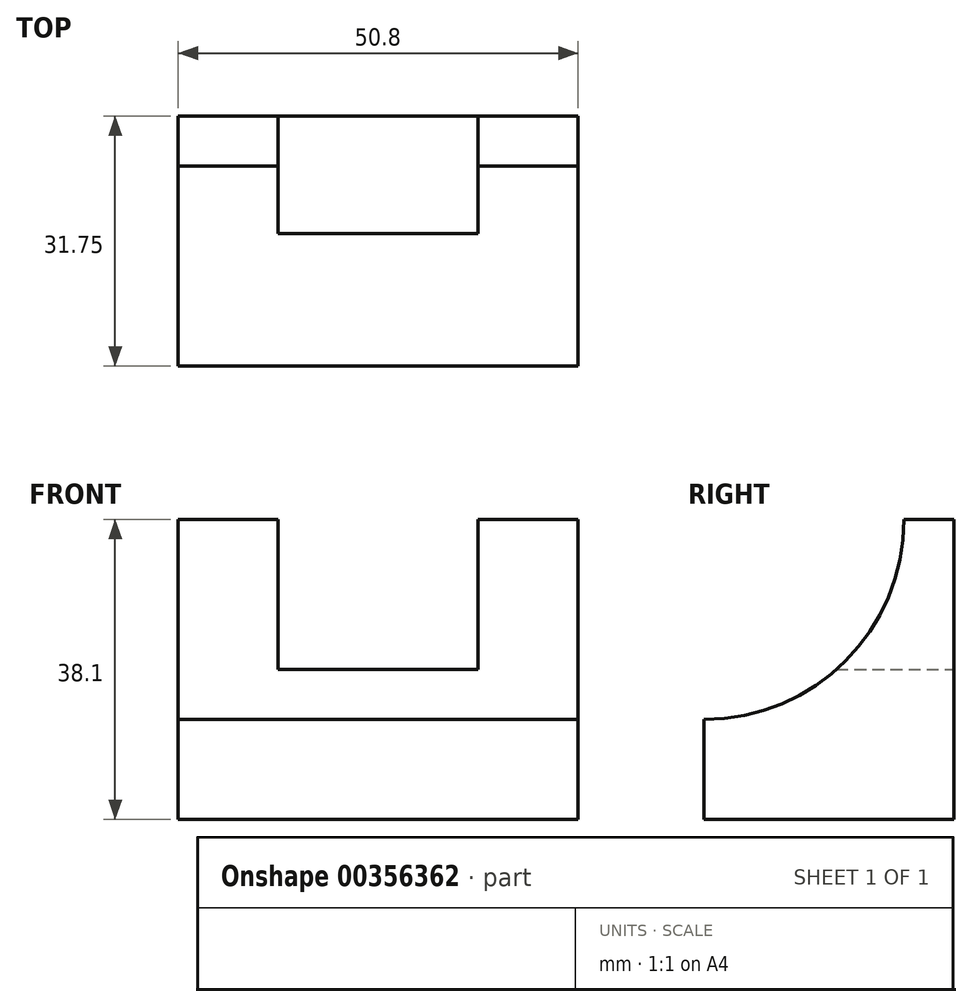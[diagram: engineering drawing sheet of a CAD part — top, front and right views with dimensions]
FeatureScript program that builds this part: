
annotation { "Feature Type Name" : "Feature", "Feature Type Description" : "" }
export const myFeature = defineFeature(function(context is Context, id is Id, definition is map)
    precondition{}
    {
        {
            var Q0;
            Q0=qCreatedBy(makeId("Right.planeOp"),FACE);
            var sketch = newSketch(context, id + "F0", { "sketchPlane" : qUnion([Q0])});
            skLineSegment(sketch, "E0", {"start": v(4.89, 14.1) * mm, "end": v(4.89, 1.4) * mm});
            skLineSegment(sketch, "E1", {"start": v(4.89, 1.4) * mm, "end": v(36.64, 1.4) * mm});
            skLineSegment(sketch, "E2", {"start": v(36.64, 1.4) * mm, "end": v(36.64, 39.5) * mm});
            skLineSegment(sketch, "E3", {"start": v(36.64, 39.5) * mm, "end": v(30.29, 39.5) * mm});
            skLineSegment(sketch, "E4", {"start": v(30.29, 39.5) * mm, "end": v(30.29, 39.5) * mm});
            skLineSegment(sketch, "E5", {"start": v(4.89, 14.1) * mm, "end": v(4.89, 14.1) * mm});
            skPoint(sketch, "E6.visualSharp", {"position": v(30.29, 14.1) * mm});
            skArc(sketch, "E6.filletArc", {"start": v(4.89, 14.1) * mm, "mid": v(22.85, 21.53) * mm, "end": v(30.29, 39.5) * mm});
            skSolve(sketch);
        }
        {
            var Q0;
            Q0=makeQuery(id+"F0.imprint","IMPRINT",FACE,{"disambiguationData":[TD([[makeQuery(id+"F0.imprint","IMPRINT",EDGE,{"derivedFrom":sQuery(id+"F0.wireOp",EDGE,"E0")}),1.0]])]});
            extrude(context, id + "F1", {"entities" : qUnion([Q0]), "depth" : 50.8 * mm});
        }
        {
            var Q0;
            Q0=makeQuery(id+"F1.opExtrude","SWEPT_FACE",FACE,{"disambiguationData":[OSD([sQuery(id+"F0.wireOp",EDGE,"E2")])]});
            var sketch = newSketch(context, id + "F2", { "sketchPlane" : qUnion([Q0])});
            skLineSegment(sketch, "E7", {"start": v(-38.1, 39.5) * mm, "end": v(-38.1, 20.44) * mm});
            skLineSegment(sketch, "E8", {"start": v(-38.1, 20.44) * mm, "end": v(-12.7, 20.44) * mm});
            skLineSegment(sketch, "E9", {"start": v(-12.7, 20.44) * mm, "end": v(-12.7, 39.5) * mm});
            skSolve(sketch);
        }
        {
            var Q0;
            {var subQ0=sQuery(id+"F2.wireOp",EDGE,"E7");Q0=makeQuery(id+"F2.imprint","IMPRINT",FACE,{"disambiguationData":[TD([[makeQuery(id+"F2.imprint","IMPRINT",EDGE,{"derivedFrom":subQ0}),1.0]])]});}
            extrude(context, id + "F3", {"entities" : qUnion([Q0]), "operationType" : NewBodyOperationType.REMOVE, "oppositeDirection" : true, "depth" : 25.4 * mm});
        }
    });
